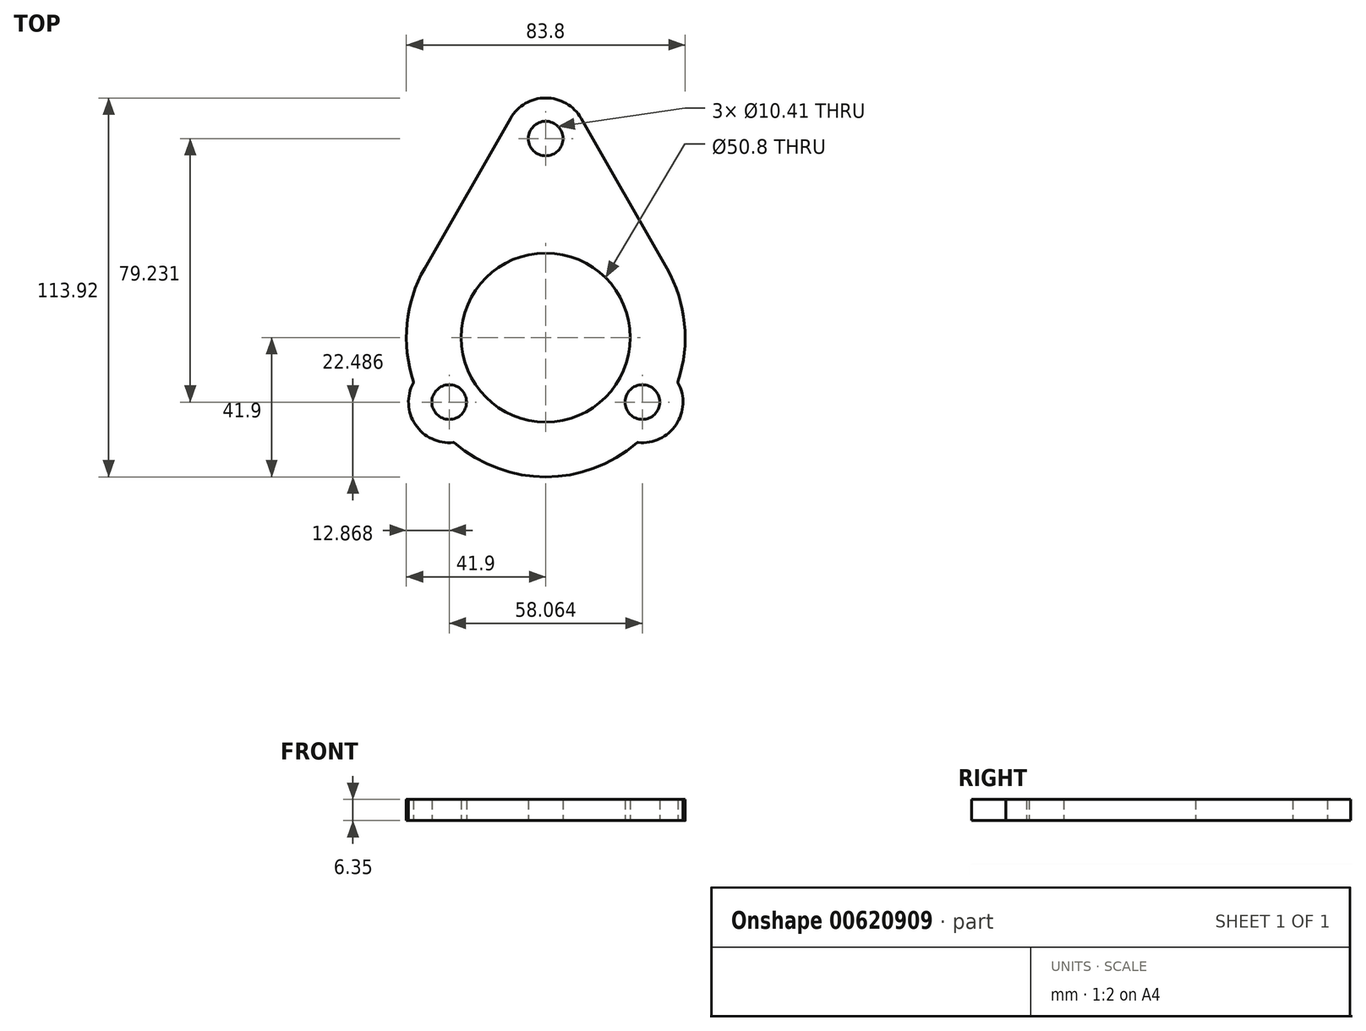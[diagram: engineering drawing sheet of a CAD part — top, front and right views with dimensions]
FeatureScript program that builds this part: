
annotation { "Feature Type Name" : "Feature", "Feature Type Description" : "" }
export const myFeature = defineFeature(function(context is Context, id is Id, definition is map)
    precondition{}
    {
        {
            var Q0;
            Q0=qCreatedBy(makeId("Top.planeOp"),FACE);
            var sketch = newSketch(context, id + "F0", { "sketchPlane" : qUnion([Q0])});
            skCircle(sketch, "E0", {"center": v(0, 0) * mm, "radius": 25.4 * mm});
            skLineSegment(sketch, "E1", {"start": v(0, 25.4) * mm, "end": v(0, 54.61) * mm, "construction": true});
            skCircle(sketch, "E2", {"center": v(0, 59.82) * mm, "radius": 5.2 * mm});
            skLineSegment(sketch, "E3", {"start": v(0, 54.61) * mm, "end": v(0, 59.82) * mm, "construction": true});
            skArc(sketch, "E4.0", {"start": v(10.6, 65.88) * mm, "mid": v(0, 72.02) * mm, "end": v(-10.6, 65.88) * mm});
            skArc(sketch, "E5.0", {"start": v(-36.37, 20.8) * mm, "mid": v(-41.7, 4.14) * mm, "end": v(-39.75, -13.24) * mm});
            skLineSegment(sketch, "E6", {"start": v(21.11, -14.12) * mm, "end": v(24.7, -16.52) * mm, "construction": true});
            skLineSegment(sketch, "E7", {"start": v(22.88, -11.48) * mm, "end": v(19.35, -16.76) * mm, "construction": true});
            skCircle(sketch, "E8", {"center": v(29.03, -19.41) * mm, "radius": 5.2 * mm});
            skLineSegment(sketch, "E9", {"start": v(0, 0) * mm, "end": v(0, -19.41) * mm, "construction": true});
            skLineSegment(sketch, "E10", {"start": v(-29.03, -19.41) * mm, "end": v(29.03, -19.41) * mm, "construction": true});
            skCircle(sketch, "E11", {"center": v(-29.03, -19.41) * mm, "radius": 5.2 * mm});
            skLineSegment(sketch, "E12", {"start": v(-23.83, -19.41) * mm, "end": v(23.83, -19.41) * mm, "construction": true});
            skLineSegment(sketch, "E13", {"start": v(22.94, -19.16) * mm, "end": v(26.47, -13.88) * mm, "construction": true});
            skArc(sketch, "E14.0", {"start": v(-39.79, -13.64) * mm, "mid": v(-39.18, -26.2) * mm, "end": v(-27.8, -31.56) * mm});
            skArc(sketch, "E15.0", {"start": v(16.83, -19.02) * mm, "mid": v(16.83, -19.22) * mm, "end": v(16.83, -19.41) * mm});
            skLineSegment(sketch, "E16", {"start": v(36.37, 20.8) * mm, "end": v(10.6, 65.88) * mm});
            skLineSegment(sketch, "E17", {"start": v(-10.6, 65.88) * mm, "end": v(-36.37, 20.8) * mm});
            skArc(sketch, "E18.trimOffspring", {"start": v(27.8, -31.56) * mm, "mid": v(39.18, -26.2) * mm, "end": v(39.79, -13.64) * mm});
            skArc(sketch, "E19.trimOffspring", {"start": v(39.75, -13.24) * mm, "mid": v(41.7, 4.14) * mm, "end": v(36.37, 20.8) * mm});
            skArc(sketch, "E20.trimOffspring", {"start": v(-16.83, -19.41) * mm, "mid": v(-16.83, -19.22) * mm, "end": v(-16.83, -19.02) * mm});
            skArc(sketch, "E21.trimOffspring", {"start": v(-27.42, -31.68) * mm, "mid": v(0, -41.9) * mm, "end": v(27.42, -31.68) * mm});
            skPoint(sketch, "E22.visualSharp", {"position": v(39.68, -13.45) * mm});
            skArc(sketch, "E22.filletArc", {"start": v(39.75, -13.24) * mm, "mid": v(39.73, -13.44) * mm, "end": v(39.79, -13.64) * mm});
            skPoint(sketch, "E23.visualSharp", {"position": v(27.59, -31.53) * mm});
            skArc(sketch, "E23.filletArc", {"start": v(27.8, -31.56) * mm, "mid": v(27.6, -31.58) * mm, "end": v(27.42, -31.68) * mm});
            skPoint(sketch, "E24.visualSharp", {"position": v(-27.59, -31.53) * mm});
            skArc(sketch, "E24.filletArc", {"start": v(-27.42, -31.68) * mm, "mid": v(-27.6, -31.58) * mm, "end": v(-27.8, -31.56) * mm});
            skPoint(sketch, "E25.visualSharp", {"position": v(-39.68, -13.45) * mm});
            skArc(sketch, "E25.filletArc", {"start": v(-39.79, -13.64) * mm, "mid": v(-39.73, -13.44) * mm, "end": v(-39.75, -13.24) * mm});
            skSolve(sketch);
        }
        {
            var Q0;
            Q0 = qSketchRegion(id + "F0", true);
            extrude(context, id + "F1", {"entities" : qUnion([Q0]), "depth" : 6.35 * mm, "offsetDistance" : 25.4 * mm});
        }
    });
